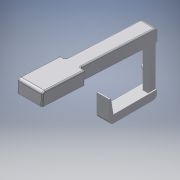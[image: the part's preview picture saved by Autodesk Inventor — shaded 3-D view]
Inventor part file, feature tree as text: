
AUTODESK INVENTOR PART (.ipt)
format: ipt  version: 2018 (Build 220112000, 112)  size: 298,496 bytes
history: native  units: mm
features: extrude x7, fillet x6, other x3, draft x1, chamfer x1
ambient origin geometry x8: Origin, YZ Plane, XZ Plane, XY Plane, X Axis, Y Axis, Z Axis, Center Point
bodies: Solid1 (feature_tree)
feature tree (18):
  other  "Key Sketch"
  extrude  "Upper Key"  Depth=10.0mm
  extrude  "Lower Key"  Depth=1.0mm
  other  "Hinge Cut Sketch"
  extrude  "Hinge Cut"  Depth=10.0mm TaperAngle=0.0deg
  extrude  "Hinge Cut 2"  Depth=3.0mm
  other  "Lever Sketch"
  extrude  "Vertical Lever"  Depth=3.0mm
  extrude  "Horizontal Lever"  Depth=33.6625mm
  extrude  "Spring Hook"  Depth=1.0mm
  draft  "FaceDraft3"
  chamfer  "Chamfer1"  Distance=3.0mm
  fillet  "Fillet9"  Radius=6.0mm
  fillet  "Fillet10"  Radius=4.0mm
  fillet  "Fillet5"  Radius=10.0mm
  fillet  "Fillet4"  [1 undecoded]
  fillet  "Fillet11"  Radius=3.0mm
  fillet  "Fillet14"  Radius=2.3mm
note: 1 required parameter value undecoded (feature->parameter linkage not recoverable at this tier; creation-order binding heuristic only, values carry confidence <= 0.55)
